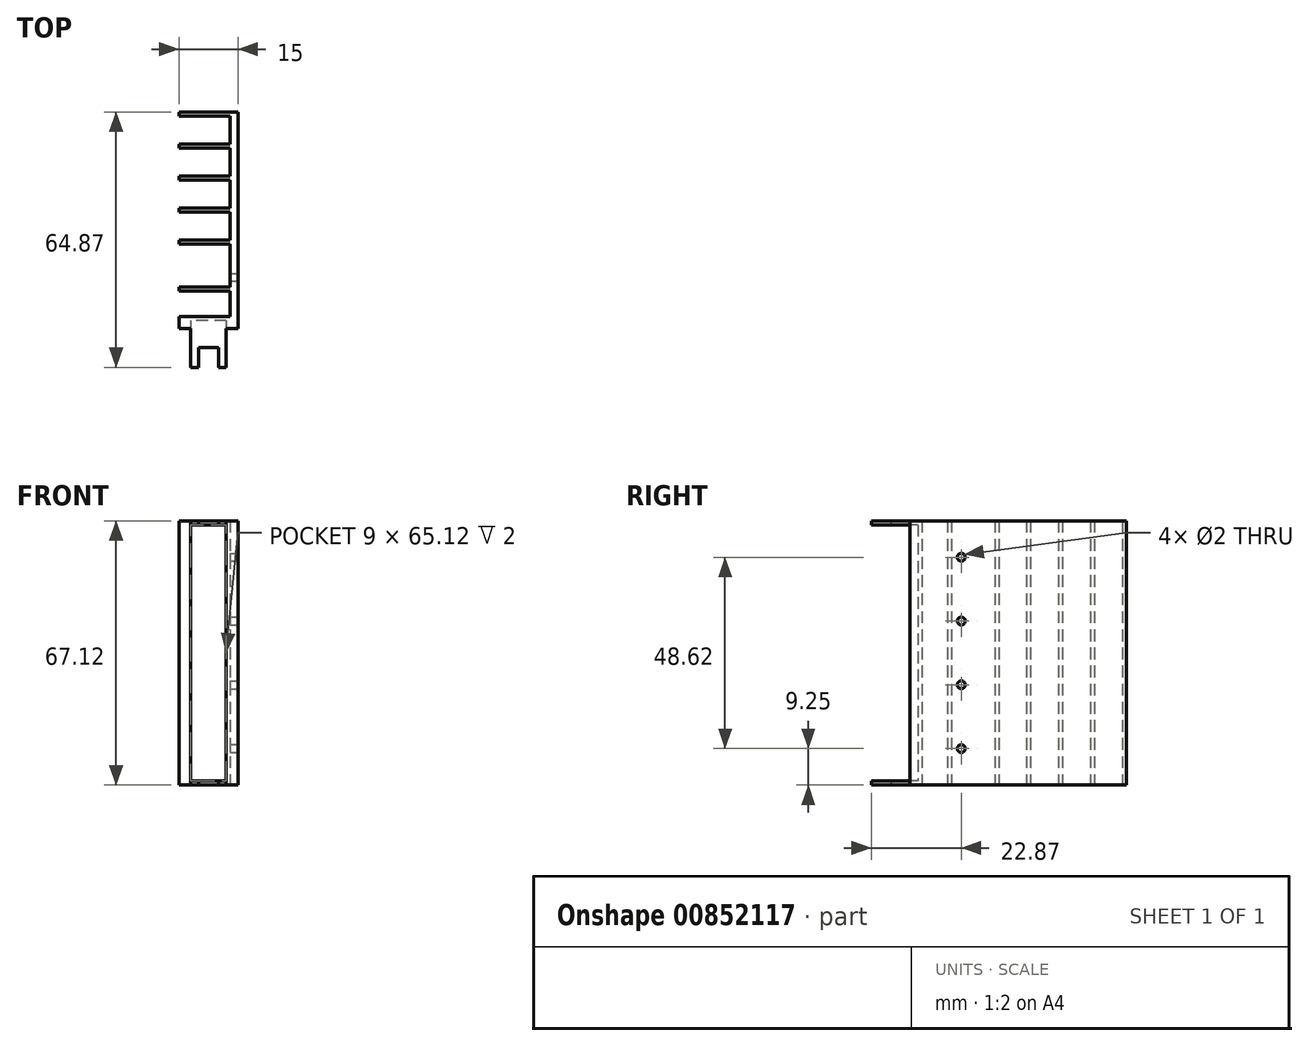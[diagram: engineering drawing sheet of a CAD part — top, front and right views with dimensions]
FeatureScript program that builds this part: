
annotation { "Feature Type Name" : "Feature", "Feature Type Description" : "" }
export const myFeature = defineFeature(function(context is Context, id is Id, definition is map)
    precondition{}
    {
        {
            var Q0;
            Q0=qCreatedBy(makeId("Top.planeOp"),FACE);
            var sketch = newSketch(context, id + "F0", { "sketchPlane" : qUnion([Q0])});
            skLineSegment(sketch, "E0", {"start": v(0, 55) * mm, "end": v(0, 0) * mm});
            skLineSegment(sketch, "E1", {"start": v(0, 0) * mm, "end": v(-3, 0) * mm});
            skLineSegment(sketch, "E2", {"start": v(-3, 0) * mm, "end": v(-3, 2) * mm});
            skLineSegment(sketch, "E3", {"start": v(-3, 2) * mm, "end": v(-12, 2) * mm});
            skLineSegment(sketch, "E4", {"start": v(-12, 2) * mm, "end": v(-12, 0) * mm});
            skLineSegment(sketch, "E5", {"start": v(-12, 0) * mm, "end": v(-15, 0) * mm});
            skLineSegment(sketch, "E6", {"start": v(-15, 0) * mm, "end": v(-15, 3) * mm});
            skLineSegment(sketch, "E7", {"start": v(-15, 3) * mm, "end": v(-2, 3) * mm});
            skLineSegment(sketch, "E8", {"start": v(-2, 3) * mm, "end": v(-2, 9.5) * mm});
            skLineSegment(sketch, "E9", {"start": v(-2, 9.5) * mm, "end": v(-15, 9.5) * mm});
            skLineSegment(sketch, "E10", {"start": v(-15, 9.5) * mm, "end": v(-15, 10.5) * mm});
            skLineSegment(sketch, "E11", {"start": v(-15, 10.5) * mm, "end": v(-2, 10.5) * mm});
            skLineSegment(sketch, "E12", {"start": v(-2, 10.5) * mm, "end": v(-2, 21.5) * mm});
            skLineSegment(sketch, "E13", {"start": v(-2, 21.5) * mm, "end": v(-15, 21.5) * mm});
            skLineSegment(sketch, "E14", {"start": v(-15, 21.5) * mm, "end": v(-15, 22.5) * mm});
            skLineSegment(sketch, "E15", {"start": v(-15, 22.5) * mm, "end": v(-2, 22.5) * mm});
            skLineSegment(sketch, "E16", {"start": v(-2, 22.5) * mm, "end": v(-2, 29.6) * mm});
            skLineSegment(sketch, "E17", {"start": v(-2, 29.6) * mm, "end": v(-15, 29.6) * mm});
            skLineSegment(sketch, "E18", {"start": v(-15, 29.6) * mm, "end": v(-15, 30.6) * mm});
            skLineSegment(sketch, "E19", {"start": v(-15, 30.6) * mm, "end": v(-2, 30.6) * mm});
            skLineSegment(sketch, "E20", {"start": v(-2, 30.6) * mm, "end": v(-2, 37.7) * mm});
            skLineSegment(sketch, "E21", {"start": v(-2, 37.7) * mm, "end": v(-15, 37.7) * mm});
            skLineSegment(sketch, "E22", {"start": v(-15, 37.7) * mm, "end": v(-15, 38.7) * mm});
            skLineSegment(sketch, "E23", {"start": v(-15, 38.7) * mm, "end": v(-2, 38.7) * mm});
            skLineSegment(sketch, "E24", {"start": v(-2, 38.7) * mm, "end": v(-2, 45.8) * mm});
            skLineSegment(sketch, "E25", {"start": v(-2, 45.8) * mm, "end": v(-15, 45.8) * mm});
            skLineSegment(sketch, "E26", {"start": v(-15, 45.8) * mm, "end": v(-15, 46.8) * mm});
            skLineSegment(sketch, "E27", {"start": v(-15, 46.8) * mm, "end": v(-2, 46.8) * mm});
            skLineSegment(sketch, "E28", {"start": v(-2, 46.8) * mm, "end": v(-2, 53.9) * mm});
            skLineSegment(sketch, "E29", {"start": v(-2, 53.9) * mm, "end": v(-15, 53.9) * mm});
            skLineSegment(sketch, "E30", {"start": v(-15, 53.9) * mm, "end": v(-15, 54.9) * mm});
            skLineSegment(sketch, "E31", {"start": v(0, 55) * mm, "end": v(-15, 55) * mm});
            skLineSegment(sketch, "E32", {"start": v(-15, 55) * mm, "end": v(-15, 54.9) * mm});
            skLineSegment(sketch, "E33", {"start": v(-3, 0) * mm, "end": v(-3, -9.87) * mm});
            skLineSegment(sketch, "E34", {"start": v(-3, -9.87) * mm, "end": v(-5, -9.87) * mm});
            skLineSegment(sketch, "E35", {"start": v(-5, -9.87) * mm, "end": v(-5, -4.87) * mm});
            skLineSegment(sketch, "E36", {"start": v(-12, -9.87) * mm, "end": v(-10, -9.87) * mm});
            skLineSegment(sketch, "E37", {"start": v(-10, -9.87) * mm, "end": v(-10, -4.87) * mm});
            skLineSegment(sketch, "E38", {"start": v(-10, -4.87) * mm, "end": v(-5, -4.87) * mm});
            skLineSegment(sketch, "E39", {"start": v(-12, -9.87) * mm, "end": v(-12, 0) * mm});
            skSolve(sketch);
        }
        {
            var Q0;
            Q0=makeQuery(id+"F0.imprint","IMPRINT",FACE,{"disambiguationData":[TD([[makeQuery(id+"F0.imprint","IMPRINT",EDGE,{"derivedFrom":sQuery(id+"F0.wireOp",EDGE,"E0")}),-1.0]])]});
            extrude(context, id + "F1", {"entities" : qUnion([Q0]), "depth" : 67.12 * mm, "offsetDistance" : 25 * mm});
        }
        {
            var Q0;
            Q0=makeQuery(id+"F0.imprint","IMPRINT",FACE,{"disambiguationData":[TD([[makeQuery(id+"F0.imprint","IMPRINT",EDGE,{"derivedFrom":sQuery(id+"F0.wireOp",EDGE,"E2")}),1.0]])]});
            extrude(context, id + "F2", {"entities" : qUnion([Q0]), "operationType" : NewBodyOperationType.ADD, "depth" : 1 * mm, "offsetDistance" : 25 * mm});
        }
        {
            var Q0;
            Q0=makeQuery(id+"F0.imprint","IMPRINT",FACE,{"disambiguationData":[TD([[makeQuery(id+"F0.imprint","IMPRINT",EDGE,{"derivedFrom":sQuery(id+"F0.wireOp",EDGE,"E2")}),1.0]])]});
            extrude(context, id + "F3", {"entities" : qUnion([Q0]), "operationType" : NewBodyOperationType.ADD, "depth" : 67.12 * mm, "offsetDistance" : 25 * mm, "hasSecondDirection" : true, "secondDirectionOppositeDirection" : false, "secondDirectionDepth" : 66.12 * mm});
        }
        {
            var Q0;
            Q0=qCreatedBy(makeId("Right.planeOp"),FACE);
            var sketch = newSketch(context, id + "F4", { "sketchPlane" : qUnion([Q0])});
            skCircle(sketch, "E40", {"center": v(13, 57.87) * mm, "radius": 1 * mm});
            skCircle(sketch, "E41", {"center": v(13, 41.66) * mm, "radius": 1 * mm});
            skCircle(sketch, "E42", {"center": v(13, 25.46) * mm, "radius": 1 * mm});
            skCircle(sketch, "E43", {"center": v(13, 9.25) * mm, "radius": 1 * mm});
            skSolve(sketch);
        }
        {
            var Q0;
            Q0=sQuery(id+"F4.wireOp",VERTEX,"E40.center");
            var Q1;
            Q1=sQuery(id+"F4.wireOp",VERTEX,"E41.center");
            var Q2;
            Q2=sQuery(id+"F4.wireOp",VERTEX,"E42.center");
            var Q3;
            Q3=sQuery(id+"F4.wireOp",VERTEX,"E43.center");
            var Q4;
            Q4=makeQuery(id+"F1.opExtrude","SWEPT_BODY",BODY,{"disambiguationData":[OSD([sQuery(id+"F0.wireOp",EDGE,"E0"),sQuery(id+"F0.wireOp",EDGE,"E1"),sQuery(id+"F0.wireOp",EDGE,"E2"),sQuery(id+"F0.wireOp",EDGE,"E3"),sQuery(id+"F0.wireOp",EDGE,"E4"),sQuery(id+"F0.wireOp",EDGE,"E5"),sQuery(id+"F0.wireOp",EDGE,"E6"),sQuery(id+"F0.wireOp",EDGE,"E7"),sQuery(id+"F0.wireOp",EDGE,"E8"),sQuery(id+"F0.wireOp",EDGE,"E9"),sQuery(id+"F0.wireOp",EDGE,"E10"),sQuery(id+"F0.wireOp",EDGE,"E11"),sQuery(id+"F0.wireOp",EDGE,"E12"),sQuery(id+"F0.wireOp",EDGE,"E13"),sQuery(id+"F0.wireOp",EDGE,"E14"),sQuery(id+"F0.wireOp",EDGE,"E15"),sQuery(id+"F0.wireOp",EDGE,"E16"),sQuery(id+"F0.wireOp",EDGE,"E17"),sQuery(id+"F0.wireOp",EDGE,"E18"),sQuery(id+"F0.wireOp",EDGE,"E19"),sQuery(id+"F0.wireOp",EDGE,"E20"),sQuery(id+"F0.wireOp",EDGE,"E21"),sQuery(id+"F0.wireOp",EDGE,"E22"),sQuery(id+"F0.wireOp",EDGE,"E23"),sQuery(id+"F0.wireOp",EDGE,"E24"),sQuery(id+"F0.wireOp",EDGE,"E25"),sQuery(id+"F0.wireOp",EDGE,"E26"),sQuery(id+"F0.wireOp",EDGE,"E27"),sQuery(id+"F0.wireOp",EDGE,"E28"),sQuery(id+"F0.wireOp",EDGE,"E29"),sQuery(id+"F0.wireOp",EDGE,"E30"),sQuery(id+"F0.wireOp",EDGE,"E31"),sQuery(id+"F0.wireOp",EDGE,"E32")])]});
            hole(context, id + "F5", {"style" : HoleStyle.SIMPLE, "endStyle" : HoleEndStyle.THROUGH, "holeDiameter" : 2 * mm, "majorDiameter" : 5 * mm, "isTappedThrough" : true, "tappedDepth" : 12 * mm, "tapClearance" : 3, "locations" : qUnion([Q0, Q1, Q2, Q3]), "scope" : qUnion([Q4])});
        }
    });
